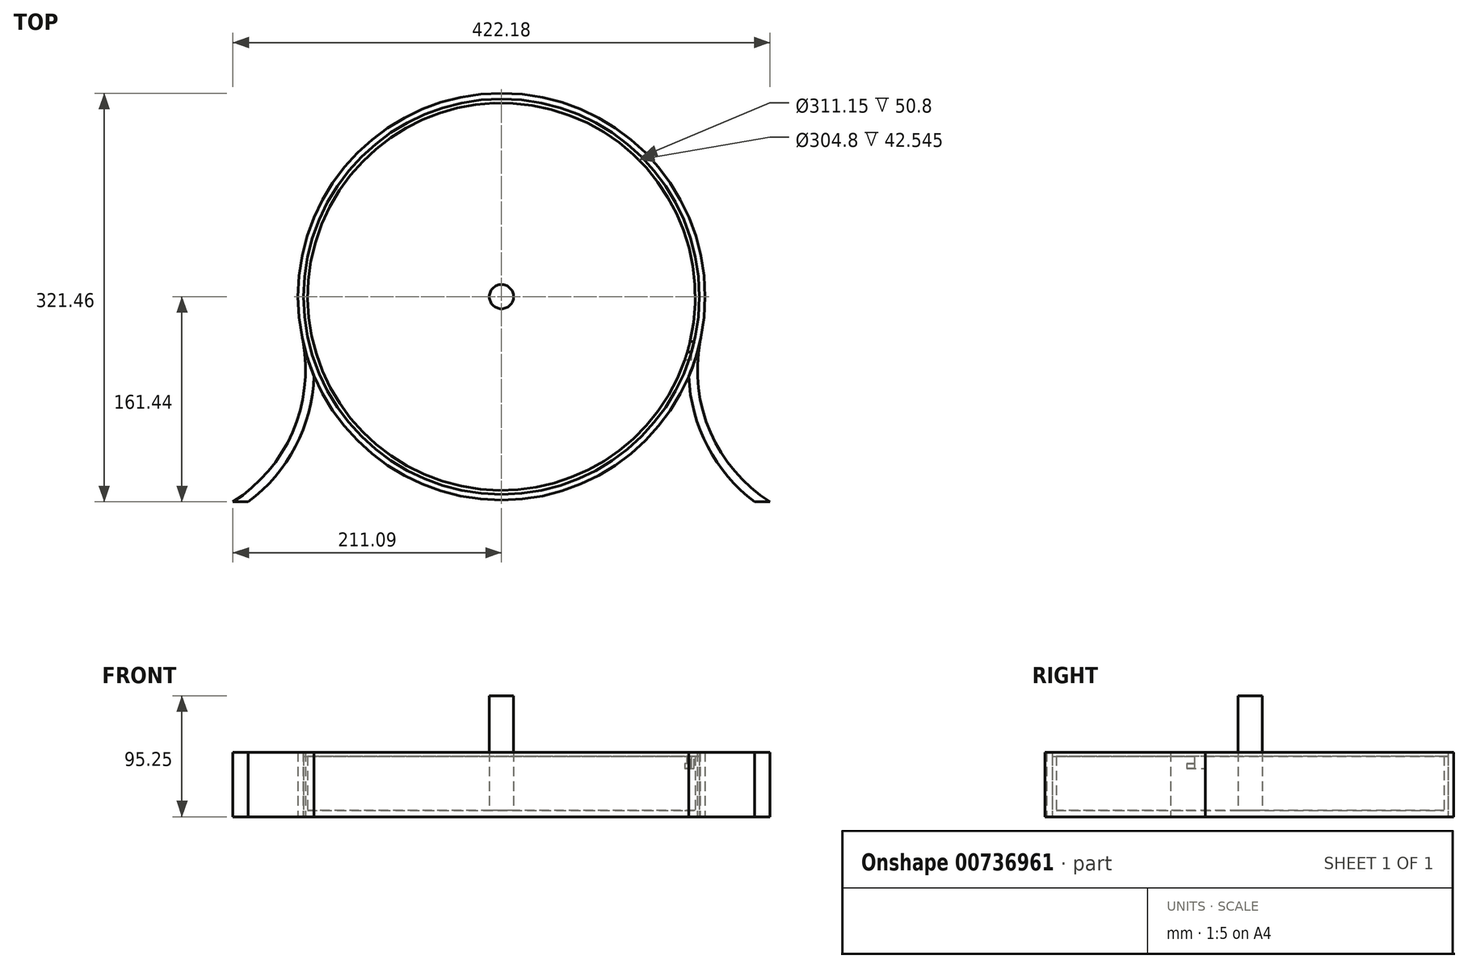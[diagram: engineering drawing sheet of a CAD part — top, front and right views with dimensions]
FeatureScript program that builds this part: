
annotation { "Feature Type Name" : "Feature", "Feature Type Description" : "" }
export const myFeature = defineFeature(function(context is Context, id is Id, definition is map)
    precondition{}
    {
        {
            var Q0;
            Q0=qCreatedBy(makeId("Top.planeOp"),FACE);
            var sketch = newSketch(context, id + "F0", { "sketchPlane" : qUnion([Q0])});
            skCircle(sketch, "E0", {"center": v(0, 0) * mm, "radius": 152.4 * mm});
            skCircle(sketch, "E1.0", {"center": v(0, 0) * mm, "radius": 160.02 * mm});
            skArc(sketch, "E2", {"start": v(-219.56, -166.36) * mm, "mid": v(-166.33, -111.18) * mm, "end": v(-156.1, -35.2) * mm});
            skArc(sketch, "E3.0", {"start": v(-216.35, -172.42) * mm, "mid": v(-160.15, -114.17) * mm, "end": v(-149.36, -33.95) * mm});
            skLineSegment(sketch, "E4", {"start": v(-156.1, -35.2) * mm, "end": v(-149.36, -33.95) * mm});
            skLineSegment(sketch, "E5", {"start": v(-219.56, -166.36) * mm, "end": v(-216.35, -172.42) * mm});
            skLineSegment(sketch, "E6.bottom", {"start": v(-273.93, -161.44) * mm, "end": v(282.58, -161.44) * mm});
            skLineSegment(sketch, "E6.top", {"start": v(-273.93, -231.73) * mm, "end": v(282.58, -231.73) * mm});
            skLineSegment(sketch, "E6.left", {"start": v(-273.93, -161.44) * mm, "end": v(-273.93, -231.73) * mm});
            skLineSegment(sketch, "E6.right", {"start": v(282.58, -161.44) * mm, "end": v(282.58, -231.73) * mm});
            skArc(sketch, "E7.MirrorCS", {"start": v(216.35, -172.42) * mm, "mid": v(160.15, -114.17) * mm, "end": v(149.36, -33.95) * mm});
            skArc(sketch, "E8.MirrorCS", {"start": v(219.56, -166.36) * mm, "mid": v(166.33, -111.18) * mm, "end": v(156.1, -35.2) * mm});
            skLineSegment(sketch, "E9.MirrorCS", {"start": v(219.56, -166.36) * mm, "end": v(216.35, -172.42) * mm});
            skCircle(sketch, "E10", {"center": v(0, 0) * mm, "radius": 9.53 * mm});
            skCircle(sketch, "E11.0", {"center": v(0, 0) * mm, "radius": 155.58 * mm});
            skSolve(sketch);
        }
        {
            var Q0;
            {var subQ0=sQuery(id+"F0.wireOp",EDGE,"E8.MirrorCS");var subQ1=sQuery(id+"F0.wireOp",EDGE,"E1.0");var subQ2=makeQuery(id+"F0.imprint","INTERSECT",VERTEX,{"derivedFrom":[subQ1,subQ0]});Q0=makeQuery(id+"F0.imprint","IMPRINT",FACE,{"disambiguationData":[TD([[makeQuery(id+"F0.imprint","IMPRINT",EDGE,{"disambiguationData":[TD([[subQ2,1.0]])],"derivedFrom":subQ1}),-1.0]])]});}
            extrude(context, id + "F1", {"entities" : qUnion([Q0]), "depth" : 50.8 * mm, "offsetDistance" : 25.4 * mm});
        }
        {
            var Q0;
            Q0=makeQuery(id+"F0.imprint","IMPRINT",FACE,{"disambiguationData":[TD([[makeQuery(id+"F0.imprint","IMPRINT",EDGE,{"derivedFrom":sQuery(id+"F0.wireOp",EDGE,"E0")}),-1.0]])]});
            var Q1;
            {var subQ0=sQuery(id+"F0.wireOp",EDGE,"E4");Q1=makeQuery(id+"F0.imprint","IMPRINT",FACE,{"disambiguationData":[TD([[makeQuery(id+"F0.imprint","IMPRINT",EDGE,{"derivedFrom":subQ0}),-1.0]])]});}
            extrude(context, id + "F2", {"entities" : qUnion([Q0, Q1]), "operationType" : NewBodyOperationType.ADD, "depth" : 50.8 * mm, "offsetDistance" : 25.4 * mm});
        }
        {
            var Q0;
            {var subQ1=sQuery(id+"F0.wireOp",EDGE,"E1.0");var subQ3=sQuery(id+"F0.wireOp",EDGE,"E3.0");var subQ4=makeQuery(id+"F0.imprint","INTERSECT",VERTEX,{"derivedFrom":[subQ1,subQ3]});Q0=makeQuery(id+"F0.imprint","IMPRINT",FACE,{"disambiguationData":[TD([[makeQuery(id+"F0.imprint","IMPRINT",EDGE,{"disambiguationData":[TD([[subQ4,1.0]])],"derivedFrom":subQ3}),1.0]])]});}
            extrude(context, id + "F3", {"entities" : qUnion([Q0]), "operationType" : NewBodyOperationType.ADD, "depth" : 50.8 * mm, "offsetDistance" : 25.4 * mm});
        }
        {
            var Q0;
            Q0=makeQuery(id+"F0.imprint","IMPRINT",FACE,{"disambiguationData":[TD([[makeQuery(id+"F0.imprint","IMPRINT",EDGE,{"derivedFrom":sQuery(id+"F0.wireOp",EDGE,"E0")}),1.0]])]});
            extrude(context, id + "F4", {"entities" : qUnion([Q0]), "operationType" : NewBodyOperationType.ADD, "depth" : 5.08 * mm, "offsetDistance" : 25.4 * mm});
        }
        {
            var Q0;
            Q0=makeQuery(id+"F0.imprint","IMPRINT",FACE,{"disambiguationData":[TD([[makeQuery(id+"F0.imprint","IMPRINT",EDGE,{"derivedFrom":sQuery(id+"F0.wireOp",EDGE,"E10")}),1.0]])]});
            extrude(context, id + "F5", {"entities" : qUnion([Q0]), "operationType" : NewBodyOperationType.ADD, "depth" : 95.25 * mm, "offsetDistance" : 25.4 * mm});
        }
        {
            var Q0;
            {var subQ1=sQuery(id+"F0.wireOp",EDGE,"E1.0");var subQ3=sQuery(id+"F0.wireOp",EDGE,"E3.0");var subQ4=makeQuery(id+"F0.imprint","INTERSECT",VERTEX,{"derivedFrom":[subQ1,subQ3]});Q0=makeQuery(id+"F0.imprint","IMPRINT",FACE,{"disambiguationData":[TD([[makeQuery(id+"F0.imprint","IMPRINT",EDGE,{"disambiguationData":[TD([[subQ4,-1.0]])],"derivedFrom":subQ3}),1.0]])]});}
            var Q1;
            {var subQ1=sQuery(id+"F0.wireOp",EDGE,"E1.0");var subQ8=makeQuery(id+"F0.imprint","INTERSECT",VERTEX,{"derivedFrom":[subQ1,sQuery(id+"F0.wireOp",EDGE,"E8.MirrorCS")]});Q1=makeQuery(id+"F0.imprint","IMPRINT",FACE,{"disambiguationData":[TD([[makeQuery(id+"F0.imprint","IMPRINT",EDGE,{"disambiguationData":[TD([[subQ8,1.0]])],"derivedFrom":subQ1}),1.0]])]});}
            var Q2;
            {var subQ0=sQuery(id+"F0.wireOp",EDGE,"E3.0");var subQ1=sQuery(id+"F0.wireOp",EDGE,"E1.0");var subQ2=makeQuery(id+"F0.imprint","INTERSECT",VERTEX,{"derivedFrom":[subQ1,subQ0]});Q2=makeQuery(id+"F0.imprint","IMPRINT",FACE,{"disambiguationData":[TD([[makeQuery(id+"F0.imprint","IMPRINT",EDGE,{"disambiguationData":[TD([[subQ2,-1.0]])],"derivedFrom":subQ1}),1.0]])]});}
            extrude(context, id + "F6", {"entities" : qUnion([Q0, Q1, Q2]), "depth" : 50.8 * mm, "offsetDistance" : 25.4 * mm});
        }
        {
            var Q0;
            Q0=makeQuery(id+"F2.opExtrude","CAP_FACE",FACE,{"disambiguationData":[OSD([sQuery(id+"F0.wireOp",EDGE,"E0"),sQuery(id+"F0.wireOp",EDGE,"E11.0")])],"isStart":false});
            var sketch = newSketch(context, id + "F7", { "sketchPlane" : qUnion([Q0])});
            skLineSegment(sketch, "E12.bottom", {"start": v(146.02, -43.64) * mm, "end": v(151.5, -43.64) * mm});
            skLineSegment(sketch, "E12.top", {"start": v(146.02, -35.38) * mm, "end": v(151.5, -35.38) * mm});
            skLineSegment(sketch, "E12.left", {"start": v(146.02, -43.64) * mm, "end": v(146.02, -35.38) * mm});
            skLineSegment(sketch, "E12.right", {"start": v(151.5, -43.64) * mm, "end": v(151.5, -35.38) * mm});
            skSolve(sketch);
        }
        {
            var Q0;
            {var subQ0=sQuery(id+"F7.wireOp",EDGE,"E12.bottom");var subQ3=makeQuery(id+"F2.opExtrude","CAP_EDGE",EDGE,{"disambiguationData":[OSD([sQuery(id+"F0.wireOp",EDGE,"E11.0")])],"isStart":false});var subQ4=makeQuery(id+"F7.imprint","INTERSECT",VERTEX,{"derivedFrom":[subQ3,subQ0]});Q0=makeQuery(id+"F7.imprint","IMPRINT",FACE,{"disambiguationData":[TD([[makeQuery(id+"F7.imprint","IMPRINT",EDGE,{"disambiguationData":[TD([[subQ4,1.0]])],"derivedFrom":subQ0}),1.0]])]});}
            extrude(context, id + "F8", {"entities" : qUnion([Q0]), "operationType" : NewBodyOperationType.REMOVE, "oppositeDirection" : true, "depth" : 12.7 * mm, "offsetDistance" : 25.4 * mm});
        }
        {
            var Q0;
            {var subQ0=sQuery(id+"F7.wireOp",EDGE,"E12.bottom");var subQ3=makeQuery(id+"F2.opExtrude","CAP_EDGE",EDGE,{"disambiguationData":[OSD([sQuery(id+"F0.wireOp",EDGE,"E11.0")])],"isStart":false});var subQ4=makeQuery(id+"F7.imprint","INTERSECT",VERTEX,{"derivedFrom":[subQ3,subQ0]});Q0=makeQuery(id+"F7.imprint","IMPRINT",FACE,{"disambiguationData":[TD([[makeQuery(id+"F7.imprint","IMPRINT",EDGE,{"disambiguationData":[TD([[subQ4,1.0]])],"derivedFrom":subQ0}),-1.0]])]});}
            extrude(context, id + "F9", {"entities" : qUnion([Q0]), "operationType" : NewBodyOperationType.REMOVE, "oppositeDirection" : true, "depth" : 3.17 * mm, "offsetDistance" : 25.4 * mm});
        }
        {
            var Q0;
            Q0=makeQuery(id+"F8.boolean.opBoolean","COPY",FACE,{"derivedFrom":makeQuery(id+"F8.opExtrude","SWEPT_FACE",FACE,{"disambiguationData":[OSD([sQuery(id+"F7.wireOp",EDGE,"E12.bottom")])]})});
            var sketch = newSketch(context, id + "F10", { "sketchPlane" : qUnion([Q0])});
            skLineSegment(sketch, "E13.bottom", {"start": v(-149.33, 41.85) * mm, "end": v(-142, 41.85) * mm});
            skLineSegment(sketch, "E13.top", {"start": v(-149.33, 38.1) * mm, "end": v(-142, 38.1) * mm});
            skLineSegment(sketch, "E13.left", {"start": v(-149.33, 41.85) * mm, "end": v(-149.33, 38.1) * mm});
            skLineSegment(sketch, "E13.right", {"start": v(-142, 41.85) * mm, "end": v(-142, 38.1) * mm});
            skSolve(sketch);
        }
        {
            var Q0;
            Q0 = qSketchRegion(id + "F10", true);
            extrude(context, id + "F11", {"entities" : qUnion([Q0]), "operationType" : NewBodyOperationType.REMOVE, "oppositeDirection" : true, "depth" : 6.35 * mm, "offsetDistance" : 25.4 * mm});
        }
    });
